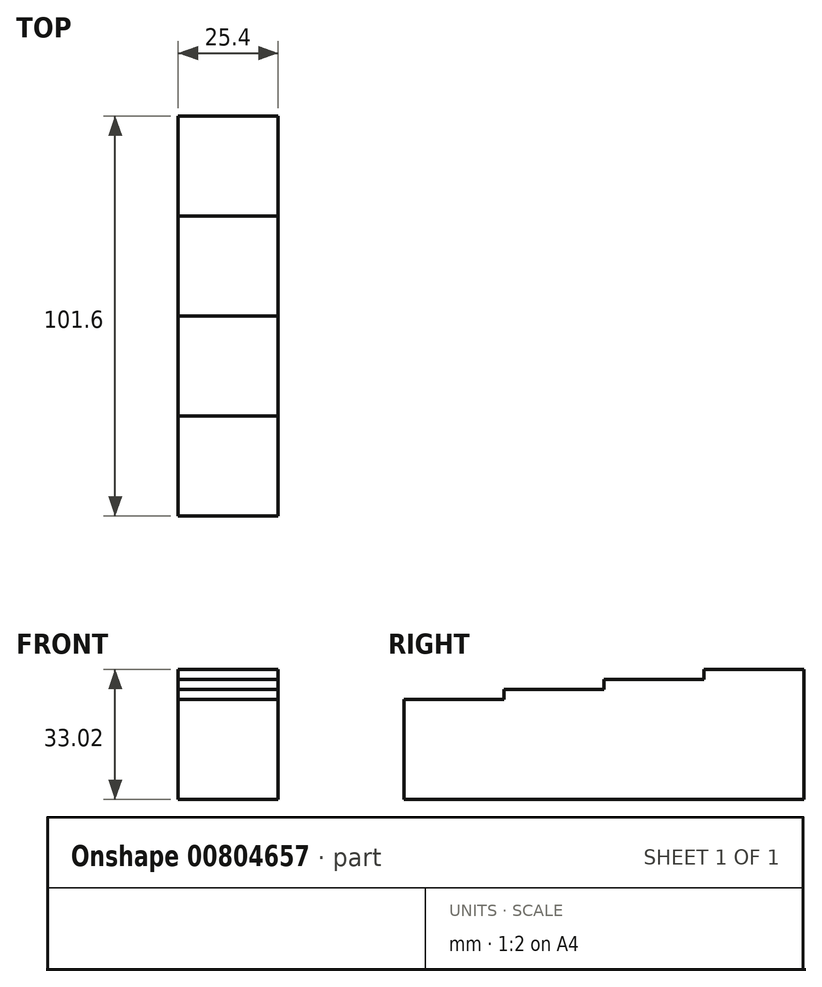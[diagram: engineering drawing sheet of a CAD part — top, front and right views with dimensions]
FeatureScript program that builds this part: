
annotation { "Feature Type Name" : "Feature", "Feature Type Description" : "" }
export const myFeature = defineFeature(function(context is Context, id is Id, definition is map)
    precondition{}
    {
        {
            var Q0;
            Q0=qCreatedBy(makeId("Front.planeOp"),FACE);
            var sketch = newSketch(context, id + "F0", { "sketchPlane" : qUnion([Q0])});
            skLineSegment(sketch, "E0.bottom", {"start": v(0, 0) * mm, "end": v(25.4, 0) * mm});
            skLineSegment(sketch, "E0.top", {"start": v(0, 25.4) * mm, "end": v(25.4, 25.4) * mm});
            skLineSegment(sketch, "E0.left", {"start": v(0, 0) * mm, "end": v(0, 25.4) * mm});
            skLineSegment(sketch, "E0.right", {"start": v(25.4, 0) * mm, "end": v(25.4, 25.4) * mm});
            skLineSegment(sketch, "E1.top", {"start": v(0, 27.94) * mm, "end": v(25.4, 27.94) * mm});
            skLineSegment(sketch, "E1.left", {"start": v(0, 25.4) * mm, "end": v(0, 27.94) * mm});
            skLineSegment(sketch, "E1.right", {"start": v(25.4, 25.4) * mm, "end": v(25.4, 27.94) * mm});
            skLineSegment(sketch, "E2.top", {"start": v(0, 30.48) * mm, "end": v(25.4, 30.48) * mm});
            skLineSegment(sketch, "E2.left", {"start": v(0, 27.94) * mm, "end": v(0, 30.48) * mm});
            skLineSegment(sketch, "E2.right", {"start": v(25.4, 27.94) * mm, "end": v(25.4, 30.48) * mm});
            skLineSegment(sketch, "E3.top", {"start": v(0, 33.02) * mm, "end": v(25.4, 33.02) * mm});
            skLineSegment(sketch, "E3.left", {"start": v(0, 30.48) * mm, "end": v(0, 33.02) * mm});
            skLineSegment(sketch, "E3.right", {"start": v(25.4, 30.48) * mm, "end": v(25.4, 33.02) * mm});
            skLineSegment(sketch, "E4.top", {"start": v(0, 35.81) * mm, "end": v(25.4, 35.81) * mm});
            skLineSegment(sketch, "E4.left", {"start": v(0, 33.02) * mm, "end": v(0, 35.81) * mm});
            skLineSegment(sketch, "E4.right", {"start": v(25.4, 33.02) * mm, "end": v(25.4, 35.81) * mm});
            skSolve(sketch);
        }
        {
            var Q0;
            Q0=makeQuery(id+"F0.imprint","IMPRINT",FACE,{"disambiguationData":[TD([[makeQuery(id+"F0.imprint","IMPRINT",EDGE,{"derivedFrom":sQuery(id+"F0.wireOp",EDGE,"E0.bottom")}),1.0]])]});
            extrude(context, id + "F1", {"entities" : qUnion([Q0]), "depth" : 101.6 * mm, "offsetDistance" : 25.4 * mm});
        }
        {
            var Q0;
            Q0=makeQuery(id+"F0.imprint","IMPRINT",FACE,{"disambiguationData":[TD([[makeQuery(id+"F0.imprint","IMPRINT",EDGE,{"derivedFrom":sQuery(id+"F0.wireOp",EDGE,"E0.top")}),1.0]])]});
            extrude(context, id + "F2", {"entities" : qUnion([Q0]), "operationType" : NewBodyOperationType.ADD, "depth" : 76.2 * mm, "offsetDistance" : 25.4 * mm});
        }
        {
            var Q0;
            Q0=makeQuery(id+"F0.imprint","IMPRINT",FACE,{"disambiguationData":[TD([[makeQuery(id+"F0.imprint","IMPRINT",EDGE,{"derivedFrom":sQuery(id+"F0.wireOp",EDGE,"E1.top")}),1.0]])]});
            extrude(context, id + "F3", {"entities" : qUnion([Q0]), "operationType" : NewBodyOperationType.ADD, "depth" : 50.8 * mm, "offsetDistance" : 25.4 * mm});
        }
        {
            var Q0;
            Q0=makeQuery(id+"F0.imprint","IMPRINT",FACE,{"disambiguationData":[TD([[makeQuery(id+"F0.imprint","IMPRINT",EDGE,{"derivedFrom":sQuery(id+"F0.wireOp",EDGE,"E2.top")}),1.0]])]});
            extrude(context, id + "F4", {"entities" : qUnion([Q0]), "operationType" : NewBodyOperationType.ADD, "depth" : 25.4 * mm, "offsetDistance" : 25.4 * mm});
        }
    });
